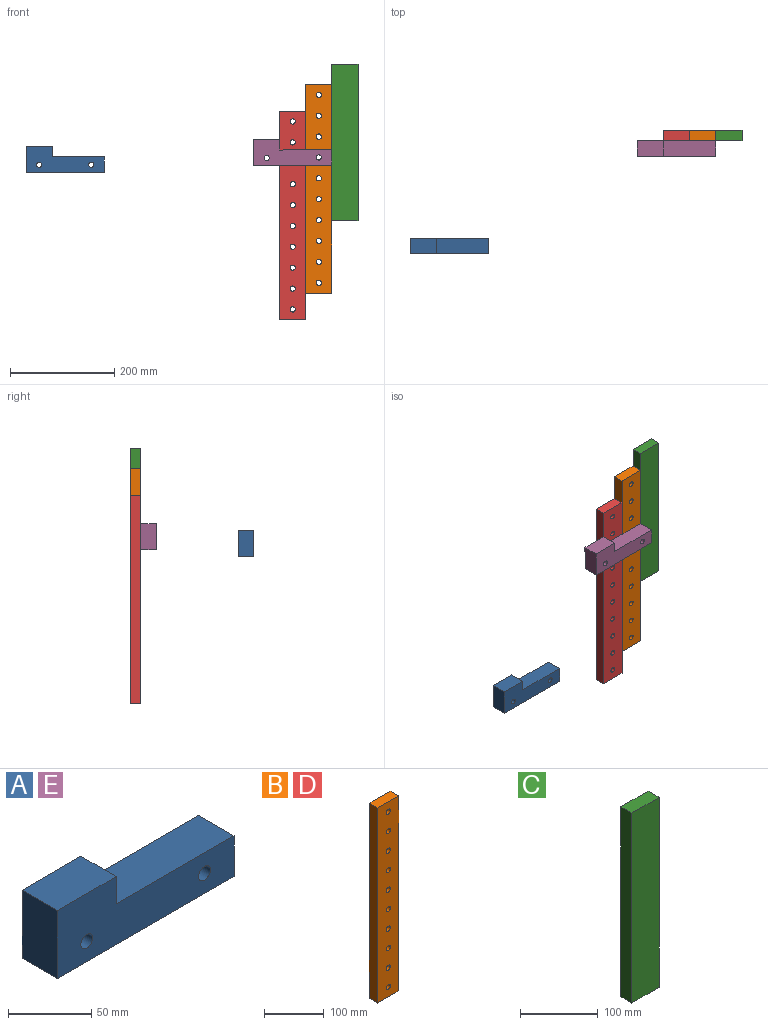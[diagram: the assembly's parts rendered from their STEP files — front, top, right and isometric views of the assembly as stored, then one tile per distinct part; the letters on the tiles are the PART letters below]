
ASSEMBLY  parts=5 mates=5
PART A: 10 faces, bbox 150x30x50 mm
  f0: plane 50x30mm, normal (0,0,1), area 1500mm2, adj f1,f7,f8,f9
  f1: plane 50x30mm, normal (-1,0,0), area 1500mm2, adj f0,f2,f8,f9
  f2: plane 150x30mm, normal (0,0,-1), area 4500mm2, adj f1,f3,f8,f9
  f3: plane 30x30mm, normal (1,0,0), area 900mm2, adj f2,f4,f8,f9
  f4: plane 100x30mm, normal (0,0,1), area 3000mm2, adj f3,f7,f8,f9
  f5: cylinder r=5mm len=30mm, axis (0,1,0), area 942.5mm2, adj f8,f9
  f6: cylinder r=5mm len=30mm, axis (0,1,0), area 942.5mm2, adj f8,f9
  f7: plane 30x20mm, normal (1,0,0), area 600mm2, adj f0,f4,f8,f9
  f8: plane 150x50mm, normal (0,-1,0), area 5342.9mm2, adj f0,f1,f2,f3,f4,f5,f6,f7
  f9: plane 150x50mm, normal (0,1,0), area 5342.9mm2, adj f0,f1,f2,f3,f4,f5,f6,f7
PART B: 16 faces, bbox 50x20x400 mm
  f0: plane 50x20mm, normal (0,0,1), area 1000mm2, adj f1,f3,f4,f5
  f1: plane 400x20mm, normal (-1,0,0), area 8000mm2, adj f0,f2,f4,f5
  f2: plane 50x20mm, normal (0,0,-1), area 1000mm2, adj f1,f3,f4,f5
  f3: plane 400x20mm, normal (1,0,0), area 8000mm2, adj f0,f2,f4,f5
  f4: plane 400x50mm, normal (0,-1,0), area 19214.6mm2, adj f0,f1,f2,f3,f6,f7,f8,f9
  f5: plane 400x50mm, normal (0,1,0), area 19214.6mm2, adj f0,f1,f2,f3,f6,f7,f8,f9
  f6: cylinder r=5mm len=20mm, axis (0,-1,0), area 628.3mm2, adj f4,f5
  f7: cylinder r=5mm len=20mm, axis (0,-1,0), area 628.3mm2, adj f4,f5
  f8: cylinder r=5mm len=20mm, axis (0,-1,0), area 628.3mm2, adj f4,f5
  f9: cylinder r=5mm len=20mm, axis (0,-1,0), area 628.3mm2, adj f4,f5
  f10: cylinder r=5mm len=20mm, axis (0,-1,0), area 628.3mm2, adj f4,f5
  f11: cylinder r=5mm len=20mm, axis (0,-1,0), area 628.3mm2, adj f4,f5
  f12: cylinder r=5mm len=20mm, axis (0,-1,0), area 628.3mm2, adj f4,f5
  f13: cylinder r=5mm len=20mm, axis (0,-1,0), area 628.3mm2, adj f4,f5
  f14: cylinder r=5mm len=20mm, axis (0,-1,0), area 628.3mm2, adj f4,f5
  f15: cylinder r=5mm len=20mm, axis (0,-1,0), area 628.3mm2, adj f4,f5
PART C: 6 faces, bbox 50x20x300 mm
  f0: plane 50x20mm, normal (0,0,1), area 1000mm2, adj f1,f3,f4,f5
  f1: plane 300x20mm, normal (-1,0,0), area 6000mm2, adj f0,f2,f4,f5
  f2: plane 50x20mm, normal (0,0,-1), area 1000mm2, adj f1,f3,f4,f5
  f3: plane 300x20mm, normal (1,0,0), area 6000mm2, adj f0,f2,f4,f5
  f4: plane 300x50mm, normal (0,-1,0), area 15000mm2, adj f0,f1,f2,f3
  f5: plane 300x50mm, normal (0,1,0), area 15000mm2, adj f0,f1,f2,f3
PART D: same geometry as B
PART E: same geometry as A
PLACE A t=(-629.56,-325.41,299.03)mm
PLACE B t=(-143.58,-138.67,-48.07)mm
PLACE C t=(-187.11,-138.67,159.95)mm fixed
PLACE D t=(-193.58,-138.67,-99.23)mm
PLACE E rot(axis=(0,-1,0),0.6deg) t=(-195.74,-138.67,313.46)mm
MATE revolute B.f12 <-> E.f5  axis (0,-1,0) through (-253.9,-158.67,103.96)mm
MATE planar C.f1 <-> B.f3  axis (-1,0,0) through (-228.9,-148.67,132.8)mm
MATE planar D.f15 <-> B.f15  axis (0,-1,0) through (-303.9,-158.67,172.8)mm
MATE planar B.f14 <-> C.f4  axis (0,-1,0) through (-253.9,-158.67,183.96)mm
MATE planar B.f1 <-> D.f3  axis (-1,0,0) through (-278.9,-148.67,43.96)mm
